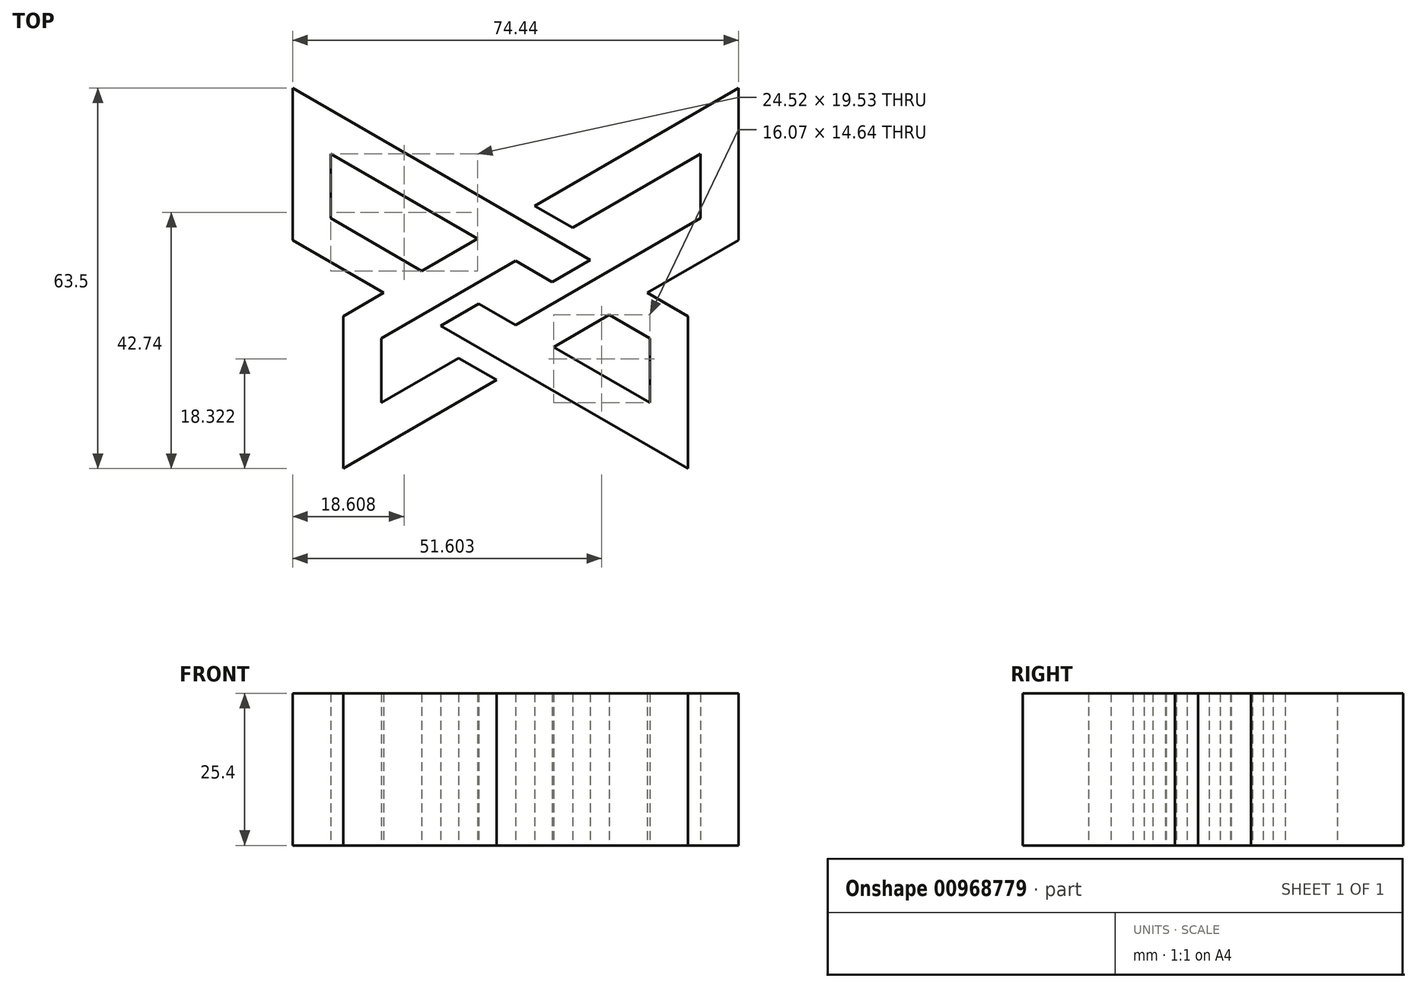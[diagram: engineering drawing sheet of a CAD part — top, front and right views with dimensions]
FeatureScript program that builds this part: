
annotation { "Feature Type Name" : "Feature", "Feature Type Description" : "" }
export const myFeature = defineFeature(function(context is Context, id is Id, definition is map)
    precondition{}
    {
        {
            var Q0;
            Q0=qCreatedBy(makeId("Top.planeOp"),FACE);
            var sketch = newSketch(context, id + "F0", { "sketchPlane" : qUnion([Q0])});
            skLineSegment(sketch, "E0", {"start": v(0, 1349.8) * mm, "end": v(0, -1190.2) * mm, "construction": true});
            skLineSegment(sketch, "E1", {"start": v(-923.2, 0) * mm, "end": v(1616.8, 0) * mm, "construction": true});
            skSolve(sketch);
        }
        {
            var Q0;
            Q0=qCreatedBy(makeId("Top.planeOp"),FACE);
            var sketch = newSketch(context, id + "F1", { "sketchPlane" : qUnion([Q0])});
            skLineSegment(sketch, "E2", {"start": v(-37.22, 34.2) * mm, "end": v(-37.22, 8.8) * mm});
            skLineSegment(sketch, "E3", {"start": v(-37.22, 8.8) * mm, "end": v(-22, 0) * mm});
            skLineSegment(sketch, "E4", {"start": v(28.77, -29.3) * mm, "end": v(28.77, -3.9) * mm});
            skLineSegment(sketch, "E5", {"start": v(28.77, -3.9) * mm, "end": v(22, 0) * mm});
            skLineSegment(sketch, "E6.MirrorCS", {"start": v(37.22, 34.2) * mm, "end": v(37.22, 8.8) * mm});
            skLineSegment(sketch, "E7.MirrorCS", {"start": v(-28.77, -3.9) * mm, "end": v(-22, 0) * mm});
            skLineSegment(sketch, "E8.MirrorCS", {"start": v(37.22, 8.8) * mm, "end": v(22, 0) * mm});
            skLineSegment(sketch, "E9.MirrorCS", {"start": v(-28.77, -29.3) * mm, "end": v(-28.77, -3.9) * mm});
            skPoint(sketch, "E10", {"position": v(-22, 0) * mm});
            skLineSegment(sketch, "E11.0", {"start": v(-30.87, 23.2) * mm, "end": v(-30.87, 12.46) * mm});
            skLineSegment(sketch, "E11.1", {"start": v(22.42, -7.57) * mm, "end": v(15.65, -3.67) * mm});
            skLineSegment(sketch, "E11.2", {"start": v(22.42, -18.3) * mm, "end": v(22.42, -7.57) * mm});
            skLineSegment(sketch, "E11.3", {"start": v(-30.87, 12.46) * mm, "end": v(-15.65, 3.67) * mm});
            skLineSegment(sketch, "E12.0", {"start": v(30.87, 12.46) * mm, "end": v(0, -5.37) * mm});
            skLineSegment(sketch, "E12.1", {"start": v(30.87, 23.2) * mm, "end": v(30.87, 12.46) * mm});
            skLineSegment(sketch, "E12.2", {"start": v(-22.42, -7.57) * mm, "end": v(0, 5.37) * mm});
            skLineSegment(sketch, "E12.3", {"start": v(-22.42, -18.3) * mm, "end": v(-22.42, -7.57) * mm});
            skLineSegment(sketch, "E13.trimOffspring", {"start": v(-9.53, -10.87) * mm, "end": v(-22.42, -18.3) * mm});
            skLineSegment(sketch, "E14.trimOffspring", {"start": v(-3.17, -14.53) * mm, "end": v(-28.77, -29.3) * mm});
            skLineSegment(sketch, "E15.trimOffspring", {"start": v(9.53, 10.87) * mm, "end": v(30.87, 23.2) * mm});
            skLineSegment(sketch, "E16.trimOffspring", {"start": v(3.18, 14.53) * mm, "end": v(37.22, 34.2) * mm});
            skLineSegment(sketch, "E17.trimOffspring", {"start": v(-15.65, 3.67) * mm, "end": v(-6.35, 9.03) * mm});
            skLineSegment(sketch, "E18.trimOffspring", {"start": v(-12.47, -5.5) * mm, "end": v(28.77, -29.3) * mm});
            skLineSegment(sketch, "E19.trimOffspring", {"start": v(-6.12, -1.83) * mm, "end": v(0, -5.37) * mm});
            skLineSegment(sketch, "E20.trimOffspring", {"start": v(-6.35, 9.03) * mm, "end": v(-30.87, 23.2) * mm});
            skLineSegment(sketch, "E21.trimOffspring", {"start": v(15.65, -3.67) * mm, "end": v(6.35, -9.03) * mm});
            skLineSegment(sketch, "E22.trimOffspring", {"start": v(6.12, 1.83) * mm, "end": v(0, 5.37) * mm});
            skLineSegment(sketch, "E23.trimOffspring", {"start": v(12.47, 5.5) * mm, "end": v(-37.22, 34.2) * mm});
            skLineSegment(sketch, "E24.trimOffspring", {"start": v(6.35, -9.03) * mm, "end": v(22.42, -18.3) * mm});
            skLineSegment(sketch, "E25", {"start": v(-12.47, -5.5) * mm, "end": v(-6.12, -1.83) * mm});
            skLineSegment(sketch, "E26", {"start": v(6.12, 1.83) * mm, "end": v(12.47, 5.5) * mm});
            skLineSegment(sketch, "E27", {"start": v(3.18, 14.53) * mm, "end": v(9.53, 10.87) * mm});
            skLineSegment(sketch, "E28", {"start": v(-9.53, -10.87) * mm, "end": v(-3.17, -14.53) * mm});
            skSolve(sketch);
        }
        {
            var Q0;
            Q0=makeQuery(id+"F1.imprint","IMPRINT",FACE,{"disambiguationData":[TD([[makeQuery(id+"F1.imprint","IMPRINT",EDGE,{"derivedFrom":sQuery(id+"F1.wireOp",EDGE,"E2")}),1.0]])]});
            var Q1;
            Q1=makeQuery(id+"F1.imprint","IMPRINT",FACE,{"disambiguationData":[TD([[makeQuery(id+"F1.imprint","IMPRINT",EDGE,{"derivedFrom":sQuery(id+"F1.wireOp",EDGE,"E4")}),1.0]])]});
            extrude(context, id + "F2", {"entities" : qUnion([Q0, Q1]), "depth" : 25.4 * mm, "offsetDistance" : 25.4 * mm});
        }
    });
